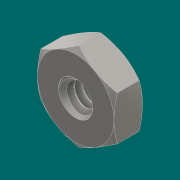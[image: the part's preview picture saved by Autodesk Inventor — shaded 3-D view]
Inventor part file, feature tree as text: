
AUTODESK INVENTOR PART (.ipt)
format: ipt  version: 2016 (Build 200138000, 138)  size: 310,784 bytes
history: native  units: mm
features: mirror x1
ambient origin geometry x8: Origin, YZ Plane, XZ Plane, XY Plane, X Axis, Y Axis, Z Axis, Center Point
bodies: Solid1 (feature_tree)
feature tree (1):
  mirror  "Mirror1"
